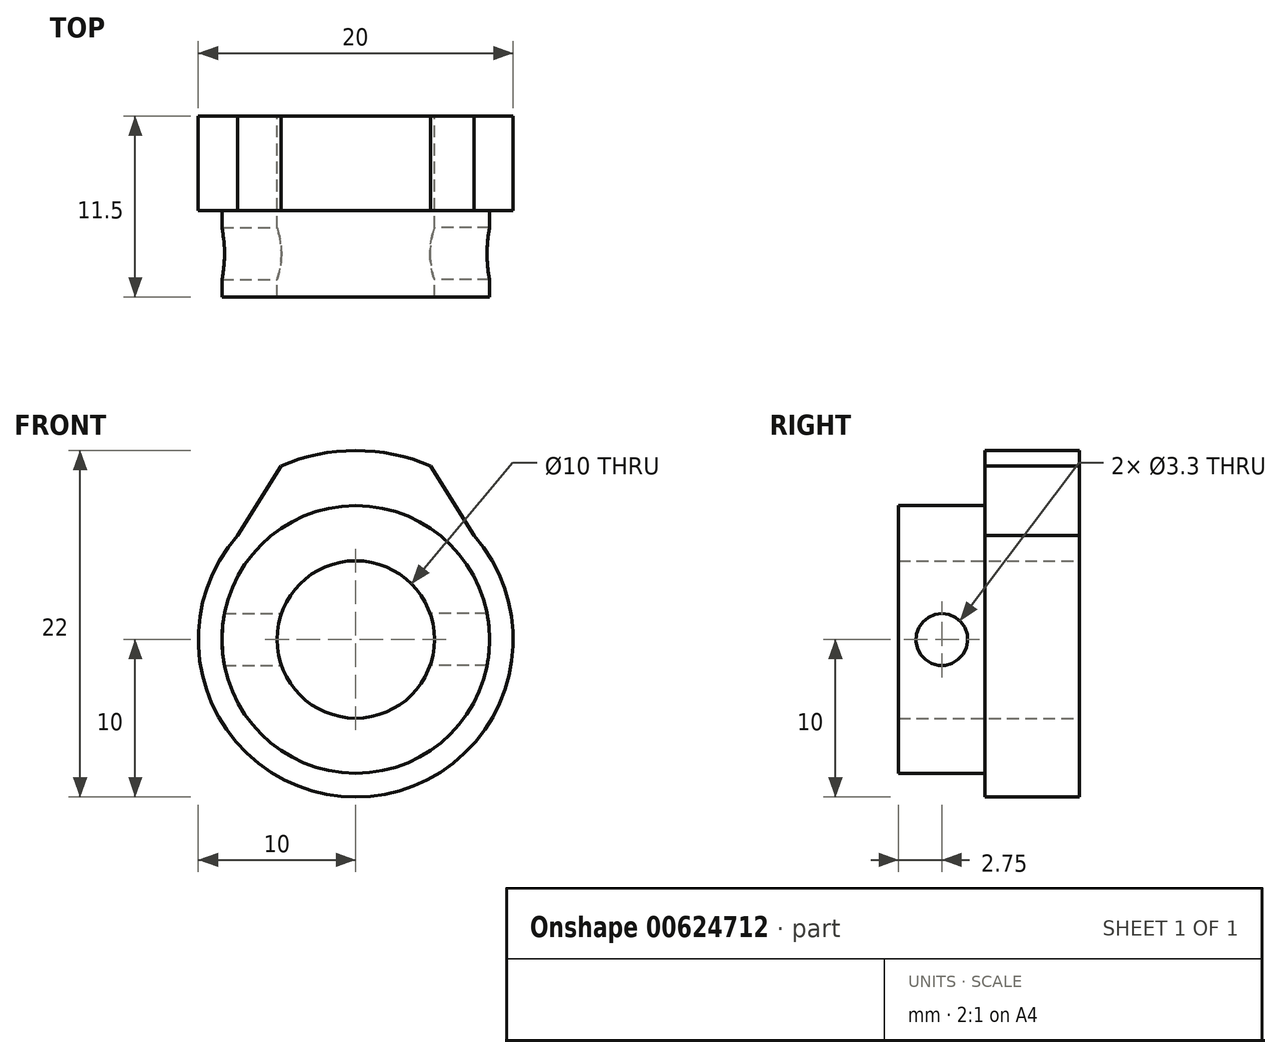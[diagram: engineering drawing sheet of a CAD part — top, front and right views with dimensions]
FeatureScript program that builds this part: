
annotation { "Feature Type Name" : "Feature", "Feature Type Description" : "" }
export const myFeature = defineFeature(function(context is Context, id is Id, definition is map)
    precondition{}
    {
        {
            var Q0;
            Q0=qCreatedBy(makeId("Front.planeOp"),FACE);
            var sketch = newSketch(context, id + "F0", { "sketchPlane" : qUnion([Q0])});
            skLineSegment(sketch, "E0", {"start": v(0, 48.05) * mm, "end": v(0, -40.77) * mm, "construction": true});
            skArc(sketch, "E1", {"start": v(-7.5, 6.61) * mm, "mid": v(0, -10) * mm, "end": v(7.5, 6.61) * mm});
            skPoint(sketch, "E2", {"position": v(-7.5, 6.61) * mm});
            skPoint(sketch, "E3", {"position": v(7.5, 6.61) * mm});
            skArc(sketch, "E4", {"start": v(4.75, 11.02) * mm, "mid": v(0, 12) * mm, "end": v(-4.75, 11.02) * mm});
            skPoint(sketch, "E5", {"position": v(-4.75, 11.02) * mm});
            skPoint(sketch, "E6", {"position": v(4.75, 11.02) * mm});
            skLineSegment(sketch, "E7", {"start": v(-4.75, 11.02) * mm, "end": v(-7.5, 6.61) * mm});
            skLineSegment(sketch, "E8", {"start": v(4.75, 11.02) * mm, "end": v(7.5, 6.61) * mm});
            skCircle(sketch, "E9", {"center": v(0, 0) * mm, "radius": 5 * mm});
            skCircle(sketch, "E10", {"center": v(0, 0) * mm, "radius": 8.5 * mm});
            skSolve(sketch);
        }
        {
            var Q0;
            Q0=makeQuery(id+"F0.imprint","IMPRINT",FACE,{"disambiguationData":[TD([[makeQuery(id+"F0.imprint","IMPRINT",EDGE,{"derivedFrom":sQuery(id+"F0.wireOp",EDGE,"E1")}),1.0]])]});
            var Q1;
            Q1=makeQuery(id+"F0.imprint","IMPRINT",FACE,{"disambiguationData":[TD([[makeQuery(id+"F0.imprint","IMPRINT",EDGE,{"derivedFrom":sQuery(id+"F0.wireOp",EDGE,"E9")}),-1.0]])]});
            extrude(context, id + "F1", {"entities" : qUnion([Q0, Q1]), "depth" : 6 * mm, "offsetDistance" : 25 * mm});
        }
        {
            var Q0;
            Q0=makeQuery(id+"F0.imprint","IMPRINT",FACE,{"disambiguationData":[TD([[makeQuery(id+"F0.imprint","IMPRINT",EDGE,{"derivedFrom":sQuery(id+"F0.wireOp",EDGE,"E9")}),-1.0]])]});
            extrude(context, id + "F2", {"entities" : qUnion([Q0]), "operationType" : NewBodyOperationType.ADD, "depth" : 11.5 * mm, "offsetDistance" : 25 * mm});
        }
        {
            var Q0;
            Q0=qCreatedBy(makeId("Right.planeOp"),FACE);
            var sketch = newSketch(context, id + "F3", { "sketchPlane" : qUnion([Q0])});
            skPoint(sketch, "E11", {"position": v(-8.75, 0) * mm});
            skSolve(sketch);
        }
        {
            var Q0;
            Q0=sQuery(id+"F3.wireOp",VERTEX,"E11");
            var Q1;
            Q1=makeQuery(id+"F1.opExtrude","SWEPT_BODY",BODY,{"disambiguationData":[OSD([sQuery(id+"F0.wireOp",EDGE,"E1"),sQuery(id+"F0.wireOp",EDGE,"E4"),sQuery(id+"F0.wireOp",EDGE,"E7"),sQuery(id+"F0.wireOp",EDGE,"E8"),sQuery(id+"F0.wireOp",EDGE,"E9")])]});
            hole(context, id + "F4", {"style" : HoleStyle.SIMPLE, "endStyle" : HoleEndStyle.THROUGH, "oppositeDirection" : true, "standardTappedOrClearance" : lookupTablePath({ "standard" : "ISO", "fit" : "Normal", "size" : "M3", "type" : "Clearance" }), "standardBlindInLast" : lookupTablePath({ "fit" : "Standard", "standard" : "ISO", "size" : "M3", "type" : "Clearance" }), "holeDiameter" : 3.3 * mm, "majorDiameter" : 3 * mm, "isTappedThrough" : true, "tappedDepth" : 12 * mm, "tapClearance" : 3, "locations" : qUnion([Q0]), "scope" : qUnion([Q1])});
        }
        {
            var Q0;
            Q0=sQuery(id+"F3.wireOp",VERTEX,"E11");
            var Q1;
            Q1=makeQuery(id+"F1.opExtrude","SWEPT_BODY",BODY,{"disambiguationData":[OSD([sQuery(id+"F0.wireOp",EDGE,"E1"),sQuery(id+"F0.wireOp",EDGE,"E4"),sQuery(id+"F0.wireOp",EDGE,"E7"),sQuery(id+"F0.wireOp",EDGE,"E8"),sQuery(id+"F0.wireOp",EDGE,"E9")])]});
            hole(context, id + "F5", {"style" : HoleStyle.SIMPLE, "endStyle" : HoleEndStyle.THROUGH, "standardTappedOrClearance" : lookupTablePath({ "standard" : "ISO", "fit" : "Normal", "size" : "M3", "type" : "Clearance" }), "standardBlindInLast" : lookupTablePath({ "fit" : "Standard", "standard" : "ISO", "size" : "M3", "type" : "Clearance" }), "holeDiameter" : 3.3 * mm, "majorDiameter" : 5 * mm, "isTappedThrough" : true, "tappedDepth" : 12 * mm, "tapClearance" : 3, "locations" : qUnion([Q0]), "scope" : qUnion([Q1])});
        }
    });
